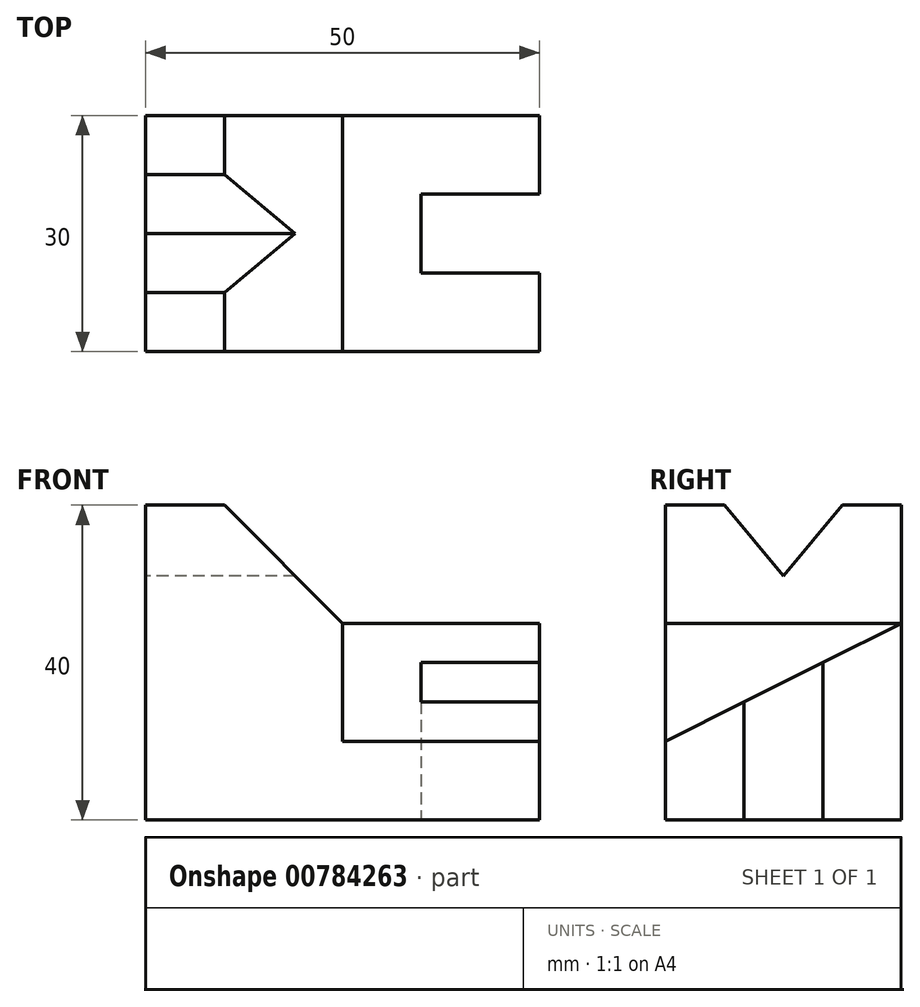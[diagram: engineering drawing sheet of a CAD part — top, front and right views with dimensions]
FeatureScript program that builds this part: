
annotation { "Feature Type Name" : "Feature", "Feature Type Description" : "" }
export const myFeature = defineFeature(function(context is Context, id is Id, definition is map)
    precondition{}
    {
        {
            var Q0;
            Q0=qCreatedBy(makeId("Front.planeOp"),FACE);
            var sketch = newSketch(context, id + "F0", { "sketchPlane" : qUnion([Q0])});
            skLineSegment(sketch, "E0.bottom", {"start": v(0, 0) * mm, "end": v(50, 0) * mm});
            skLineSegment(sketch, "E0.top", {"start": v(0, 40) * mm, "end": v(10, 40) * mm});
            skLineSegment(sketch, "E0.left", {"start": v(0, 0) * mm, "end": v(0, 40) * mm});
            skLineSegment(sketch, "E0.right", {"start": v(50, 0) * mm, "end": v(50, 25) * mm});
            skLineSegment(sketch, "E1", {"start": v(10, 40) * mm, "end": v(25, 25) * mm});
            skPoint(sketch, "E1.endSnap0", {"position": v(25, 0) * mm});
            skLineSegment(sketch, "E2", {"start": v(25, 25) * mm, "end": v(50, 25) * mm});
            skSolve(sketch);
        }
        {
            var Q0;
            Q0 = qSketchRegion(id + "F0", true);
            extrude(context, id + "F1", {"entities" : qUnion([Q0]), "depth" : 30 * mm, "offsetDistance" : 25 * mm});
        }
        {
            var Q0;
            Q0=makeQuery(id+"F1.opExtrude","SWEPT_FACE",FACE,{"disambiguationData":[OSD([sQuery(id+"F0.wireOp",EDGE,"E0.left")])]});
            var sketch = newSketch(context, id + "F2", { "sketchPlane" : qUnion([Q0])});
            skLineSegment(sketch, "E3", {"start": v(15, 40) * mm, "end": v(15, 31) * mm, "construction": true});
            skLineSegment(sketch, "E4", {"start": v(15, 31) * mm, "end": v(7.5, 40) * mm});
            skLineSegment(sketch, "E5.MirrorCS", {"start": v(15, 31) * mm, "end": v(22.5, 40) * mm});
            skLineSegment(sketch, "E6.0", {"start": v(30, 40) * mm, "end": v(0, 40) * mm});
            skSolve(sketch);
        }
        {
            var Q0;
            Q0 = qSketchRegion(id + "F2", true);
            extrude(context, id + "F3", {"entities" : qUnion([Q0]), "operationType" : NewBodyOperationType.REMOVE, "endBound" : BoundingType.THROUGH_ALL, "oppositeDirection" : true, "depth" : 25 * mm, "offsetDistance" : 25 * mm});
        }
        {
            var Q0;
            Q0=makeQuery(id+"F1.opExtrude","SWEPT_FACE",FACE,{"disambiguationData":[OSD([sQuery(id+"F0.wireOp",EDGE,"E0.right")])]});
            var sketch = newSketch(context, id + "F4", { "sketchPlane" : qUnion([Q0])});
            skLineSegment(sketch, "E7", {"start": v(0, 25) * mm, "end": v(-30, 10) * mm});
            skLineSegment(sketch, "E8", {"start": v(-20, 15) * mm, "end": v(-20, 0) * mm});
            skLineSegment(sketch, "E9", {"start": v(-10, 20) * mm, "end": v(-10, 0) * mm});
            skSolve(sketch);
        }
        {
            var Q0;
            {var subQ1=sQuery(id+"F0.wireOp",EDGE,"E0.right");var subQ6=makeQuery(id+"F1.opExtrude","SWEPT_EDGE",EDGE,{"disambiguationData":[OSD([subQ1,sQuery(id+"F0.wireOp",EDGE,"E2")])]});Q0=makeQuery(id+"F4.imprint","IMPRINT",FACE,{"disambiguationData":[TD([[makeQuery(id+"F4.imprint","IMPRINT",EDGE,{"derivedFrom":subQ6}),-1.0]])]});}
            var Q1;
            Q1=makeQuery(id+"F1.opExtrude","CAP_VERTEX",VERTEX,{"disambiguationData":[OSD([sQuery(id+"F0.wireOp",EDGE,"E1"),sQuery(id+"F0.wireOp",EDGE,"E2")])],"isStart":false});
            extrude(context, id + "F5", {"entities" : qUnion([Q0]), "operationType" : NewBodyOperationType.REMOVE, "endBound" : BoundingType.UP_TO_VERTEX, "oppositeDirection" : true, "depth" : 25 * mm, "endBoundEntityVertex" : qUnion([Q1]), "offsetDistance" : 25 * mm});
        }
        {
            var Q0;
            {var subQ0=sQuery(id+"F4.wireOp",EDGE,"E8");Q0=makeQuery(id+"F4.imprint","IMPRINT",FACE,{"disambiguationData":[TD([[makeQuery(id+"F4.imprint","IMPRINT",EDGE,{"derivedFrom":subQ0}),1.0]])]});}
            extrude(context, id + "F6", {"entities" : qUnion([Q0]), "operationType" : NewBodyOperationType.REMOVE, "oppositeDirection" : true, "depth" : 15 * mm, "offsetDistance" : 25 * mm});
        }
    });
